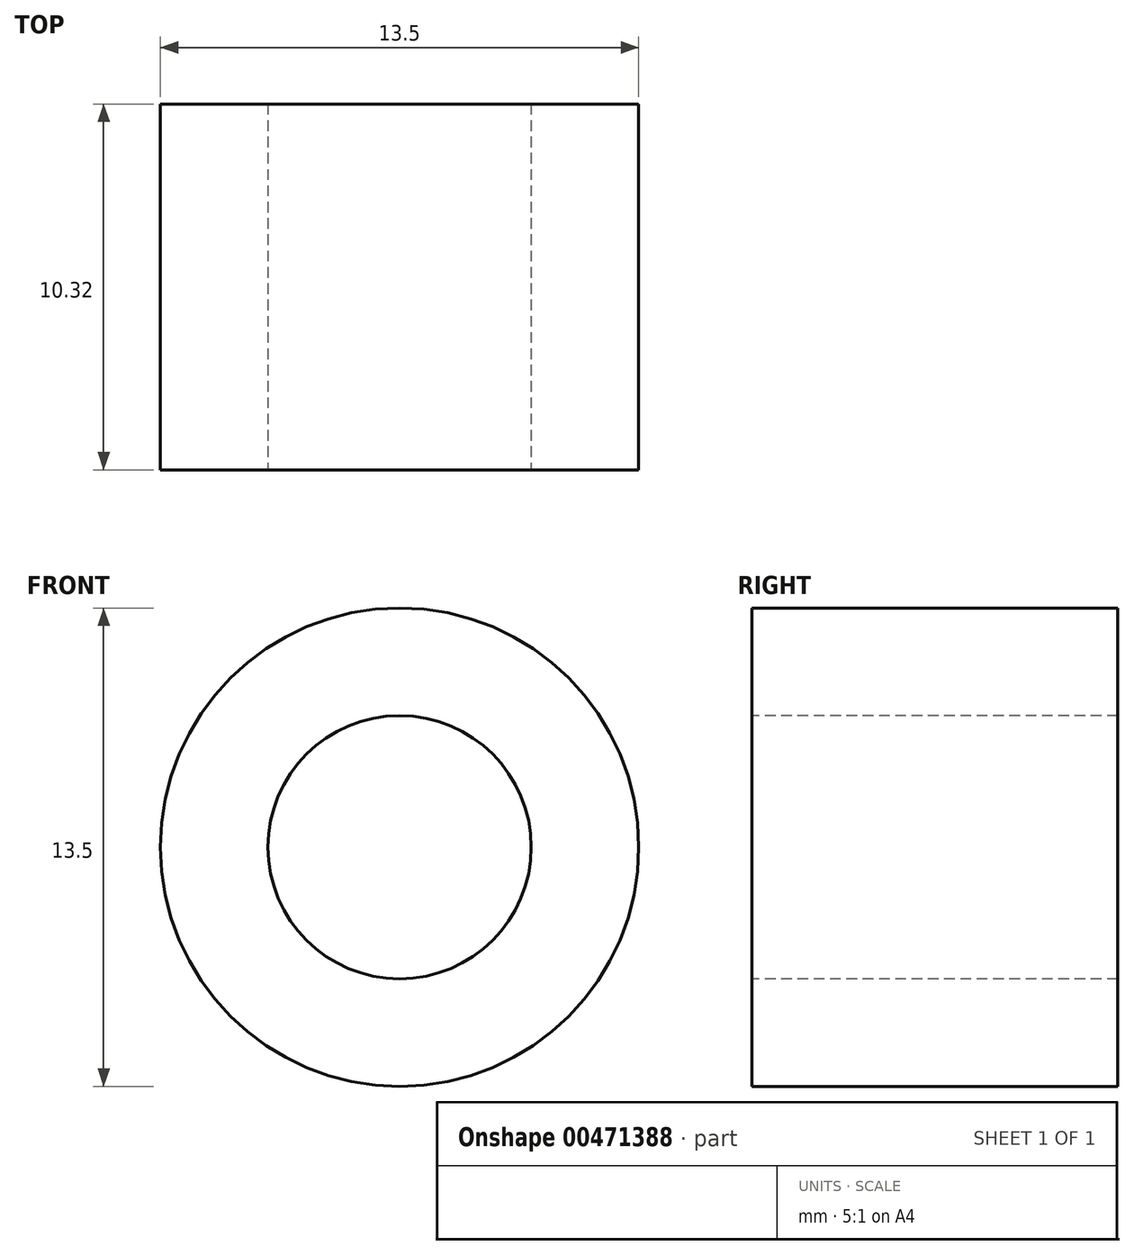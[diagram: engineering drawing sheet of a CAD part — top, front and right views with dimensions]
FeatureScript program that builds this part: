
annotation { "Feature Type Name" : "Feature", "Feature Type Description" : "" }
export const myFeature = defineFeature(function(context is Context, id is Id, definition is map)
    precondition{}
    {
        {
            var Q0;
            Q0=qCreatedBy(makeId("Right.planeOp"),FACE);
            var sketch = newSketch(context, id + "F0", { "sketchPlane" : qUnion([Q0])});
            skLineSegment(sketch, "E0.bottom", {"start": v(0, 0) * mm, "end": v(10.32, 0) * mm, "construction": true});
            skLineSegment(sketch, "E0.top", {"start": v(0, 6.75) * mm, "end": v(10.32, 6.75) * mm});
            skLineSegment(sketch, "E0.left", {"start": v(0, 3.71) * mm, "end": v(0, 6.75) * mm});
            skLineSegment(sketch, "E0.right", {"start": v(10.32, 3.71) * mm, "end": v(10.32, 6.75) * mm});
            skLineSegment(sketch, "E1", {"start": v(0, 3.71) * mm, "end": v(10.32, 3.71) * mm});
            skSolve(sketch);
        }
        {
            var Q0;
            Q0=makeQuery(id+"F0.imprint","IMPRINT",FACE,{"disambiguationData":[TD([[makeQuery(id+"F0.imprint","IMPRINT",EDGE,{"derivedFrom":sQuery(id+"F0.wireOp",EDGE,"E0.top")}),-1.0]])]});
            var Q1;
            Q1=sQuery(id+"F0.wireOp",EDGE,"E0.bottom");
            revolve(context, id + "F1", {"entities" : qUnion([Q0]), "axis" : qUnion([Q1]), "revolveType" : RevolveType.FULL});
        }
    });
